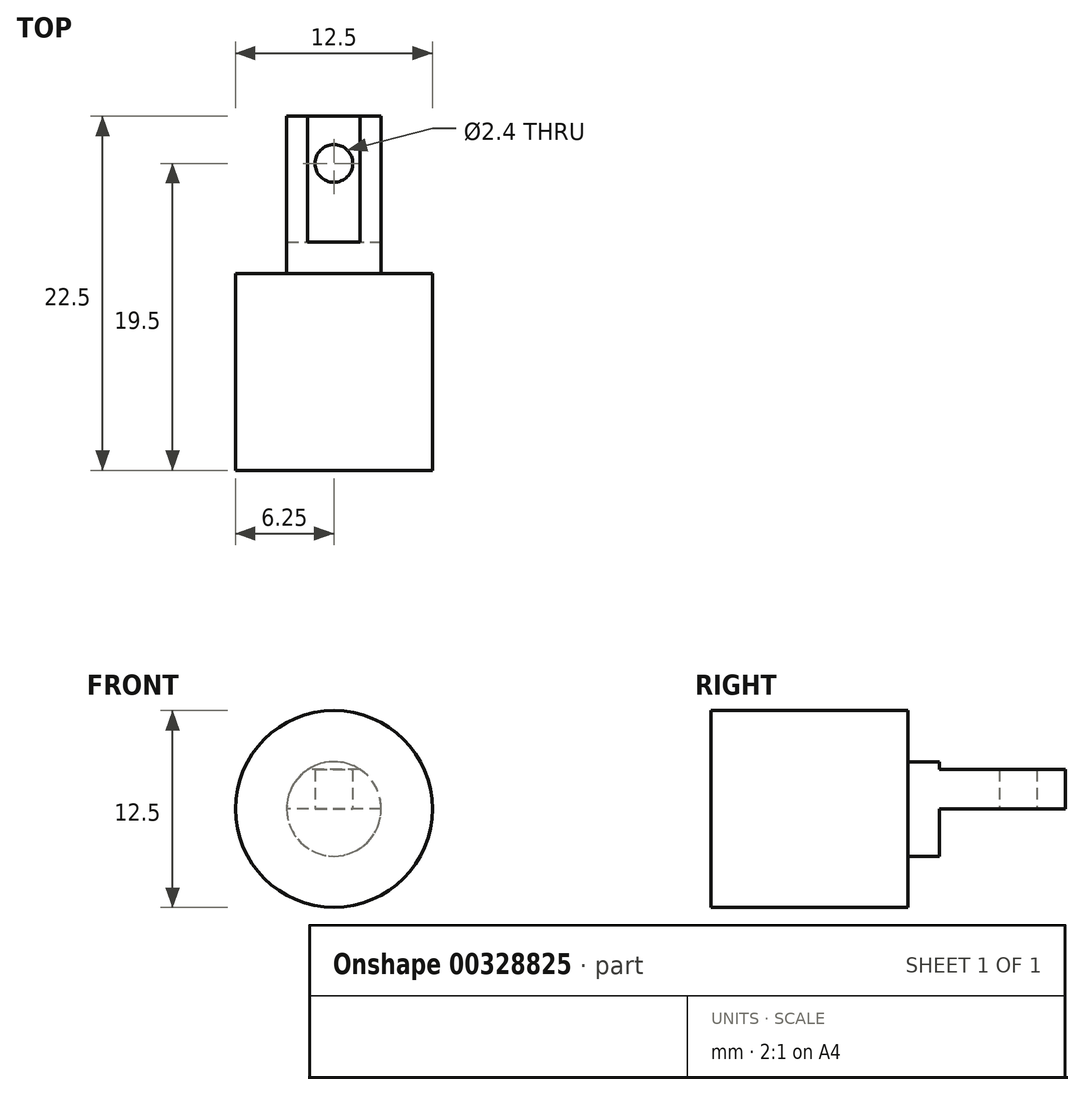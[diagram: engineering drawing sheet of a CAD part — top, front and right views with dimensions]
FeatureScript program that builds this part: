
annotation { "Feature Type Name" : "Feature", "Feature Type Description" : "" }
export const myFeature = defineFeature(function(context is Context, id is Id, definition is map)
    precondition{}
    {
        {
            var Q0;
            Q0=qCreatedBy(makeId("Right.planeOp"),FACE);
            var sketch = newSketch(context, id + "F0", { "sketchPlane" : qUnion([Q0])});
            skLineSegment(sketch, "E0", {"start": v(0, 0) * mm, "end": v(0, 6.25) * mm});
            skLineSegment(sketch, "E1", {"start": v(0, 6.25) * mm, "end": v(12.5, 6.25) * mm});
            skLineSegment(sketch, "E2", {"start": v(12.5, 6.25) * mm, "end": v(12.5, 3) * mm});
            skLineSegment(sketch, "E3", {"start": v(12.5, 3) * mm, "end": v(22.5, 3) * mm});
            skLineSegment(sketch, "E4", {"start": v(22.5, 3) * mm, "end": v(22.5, 0) * mm});
            skLineSegment(sketch, "E5", {"start": v(0, 0) * mm, "end": v(26.6, 0) * mm, "construction": true});
            skLineSegment(sketch, "E6", {"start": v(0, 0) * mm, "end": v(22.5, 0) * mm});
            skSolve(sketch);
        }
        {
            var Q0;
            Q0 = qSketchRegion(id + "F0", true);
            var Q1;
            Q1=sQuery(id+"F0.wireOp",EDGE,"E5");
            revolve(context, id + "F1", {"entities" : qUnion([Q0]), "axis" : qUnion([Q1]), "revolveType" : RevolveType.FULL});
        }
        {
            var Q0;
            Q0=qCreatedBy(makeId("Right.planeOp"),FACE);
            var sketch = newSketch(context, id + "F2", { "sketchPlane" : qUnion([Q0])});
            skLineSegment(sketch, "E7.bottom", {"start": v(14.5, 0) * mm, "end": v(24.08, 0) * mm});
            skLineSegment(sketch, "E7.top", {"start": v(14.5, -5.02) * mm, "end": v(24.08, -5.02) * mm});
            skLineSegment(sketch, "E7.left", {"start": v(14.5, 0) * mm, "end": v(14.5, -5.02) * mm});
            skLineSegment(sketch, "E7.right", {"start": v(24.08, 0) * mm, "end": v(24.08, -5.02) * mm});
            skLineSegment(sketch, "E8.bottom", {"start": v(14.5, 2.5) * mm, "end": v(24.08, 2.5) * mm});
            skLineSegment(sketch, "E8.top", {"start": v(14.5, 4.7) * mm, "end": v(24.08, 4.7) * mm});
            skLineSegment(sketch, "E8.left", {"start": v(14.5, 2.5) * mm, "end": v(14.5, 4.7) * mm});
            skLineSegment(sketch, "E8.right", {"start": v(24.08, 2.5) * mm, "end": v(24.08, 4.7) * mm});
            skSolve(sketch);
        }
        {
            var Q0;
            Q0 = qSketchRegion(id + "F2", true);
            extrude(context, id + "F3", {"entities" : qUnion([Q0]), "operationType" : NewBodyOperationType.REMOVE, "endBound" : BoundingType.THROUGH_ALL, "oppositeDirection" : true, "depth" : 25 * mm, "hasSecondDirection" : true, "secondDirectionBound" : SecondDirectionBoundingType.THROUGH_ALL, "secondDirectionOppositeDirection" : false, "secondDirectionDepth" : 25 * mm});
        }
        {
            var Q0;
            Q0=makeQuery(id+"F3.boolean.opBoolean","COPY",FACE,{"derivedFrom":makeQuery(id+"F3.opExtrude","SWEPT_FACE",FACE,{"disambiguationData":[OSD([sQuery(id+"F2.wireOp",EDGE,"E7.bottom")])]})});
            var sketch = newSketch(context, id + "F4", { "sketchPlane" : qUnion([Q0])});
            skCircle(sketch, "E9", {"center": v(0, -19.5) * mm, "radius": 1.2 * mm});
            skSolve(sketch);
        }
        {
            var Q0;
            Q0 = qSketchRegion(id + "F4", true);
            extrude(context, id + "F5", {"entities" : qUnion([Q0]), "operationType" : NewBodyOperationType.REMOVE, "endBound" : BoundingType.THROUGH_ALL, "oppositeDirection" : true, "depth" : 25 * mm});
        }
    });
